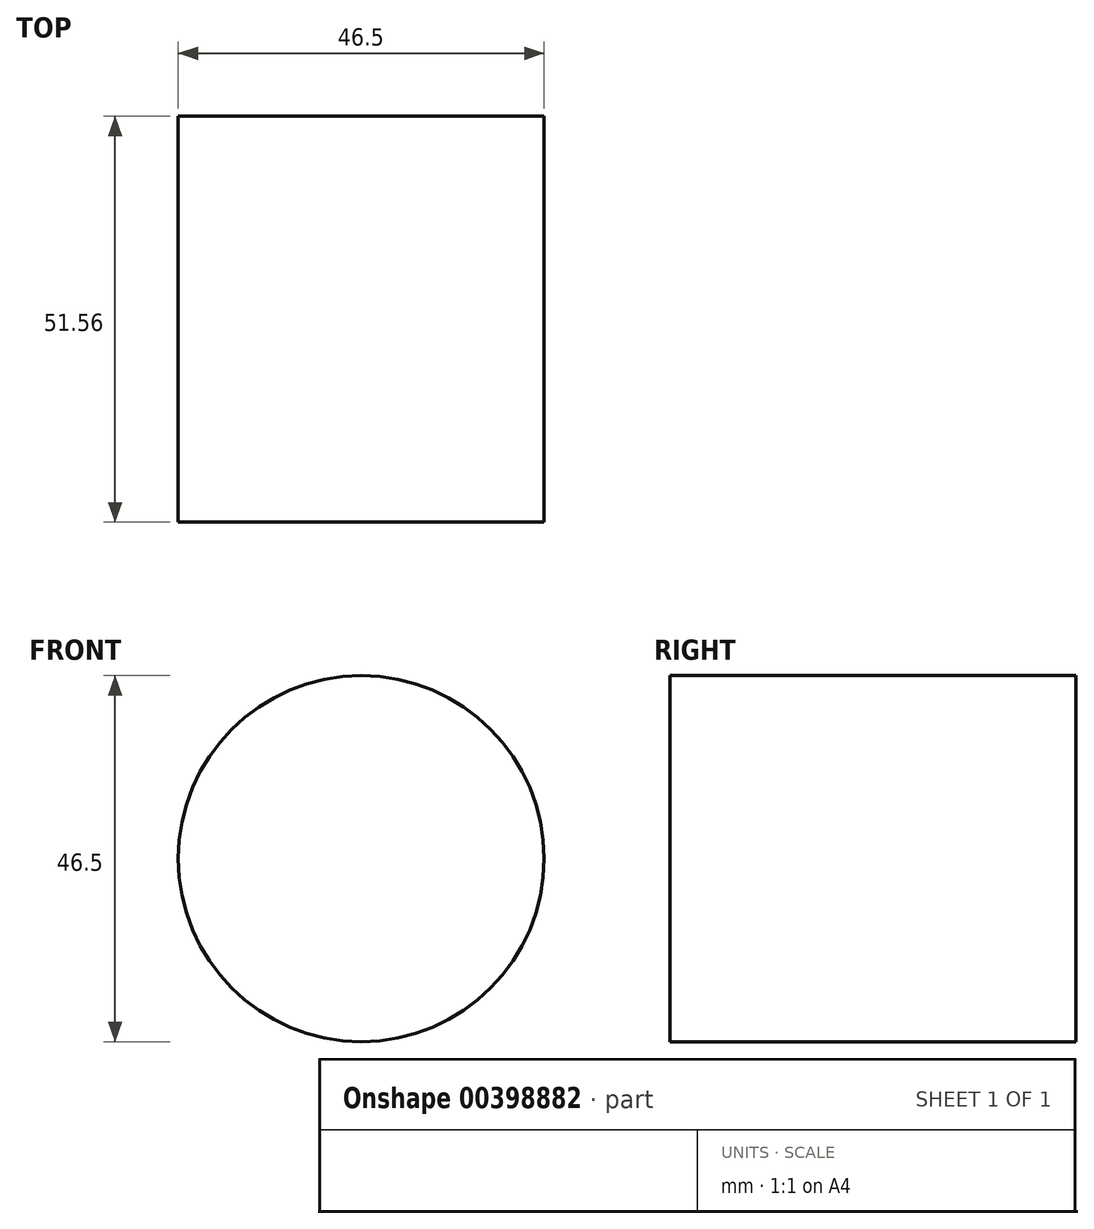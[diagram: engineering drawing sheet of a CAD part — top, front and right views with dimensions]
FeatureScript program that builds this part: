
annotation { "Feature Type Name" : "Feature", "Feature Type Description" : "" }
export const myFeature = defineFeature(function(context is Context, id is Id, definition is map)
    precondition{}
    {
        {
            var Q0;
            Q0=qCreatedBy(makeId("Front.planeOp"),FACE);
            var sketch = newSketch(context, id + "F0", { "sketchPlane" : qUnion([Q0])});
            skCircle(sketch, "E0", {"center": v(0, 0) * mm, "radius": 23.25 * mm});
            skSolve(sketch);
        }
        {
            var Q0;
            Q0=makeQuery(id+"F0.imprint","IMPRINT",FACE,{"disambiguationData":[TD([[makeQuery(id+"F0.imprint","IMPRINT",EDGE,{"derivedFrom":sQuery(id+"F0.wireOp",EDGE,"E0")}),1.0]])]});
            extrude(context, id + "F1", {"entities" : qUnion([Q0]), "depth" : 51.56 * mm});
        }
    });
